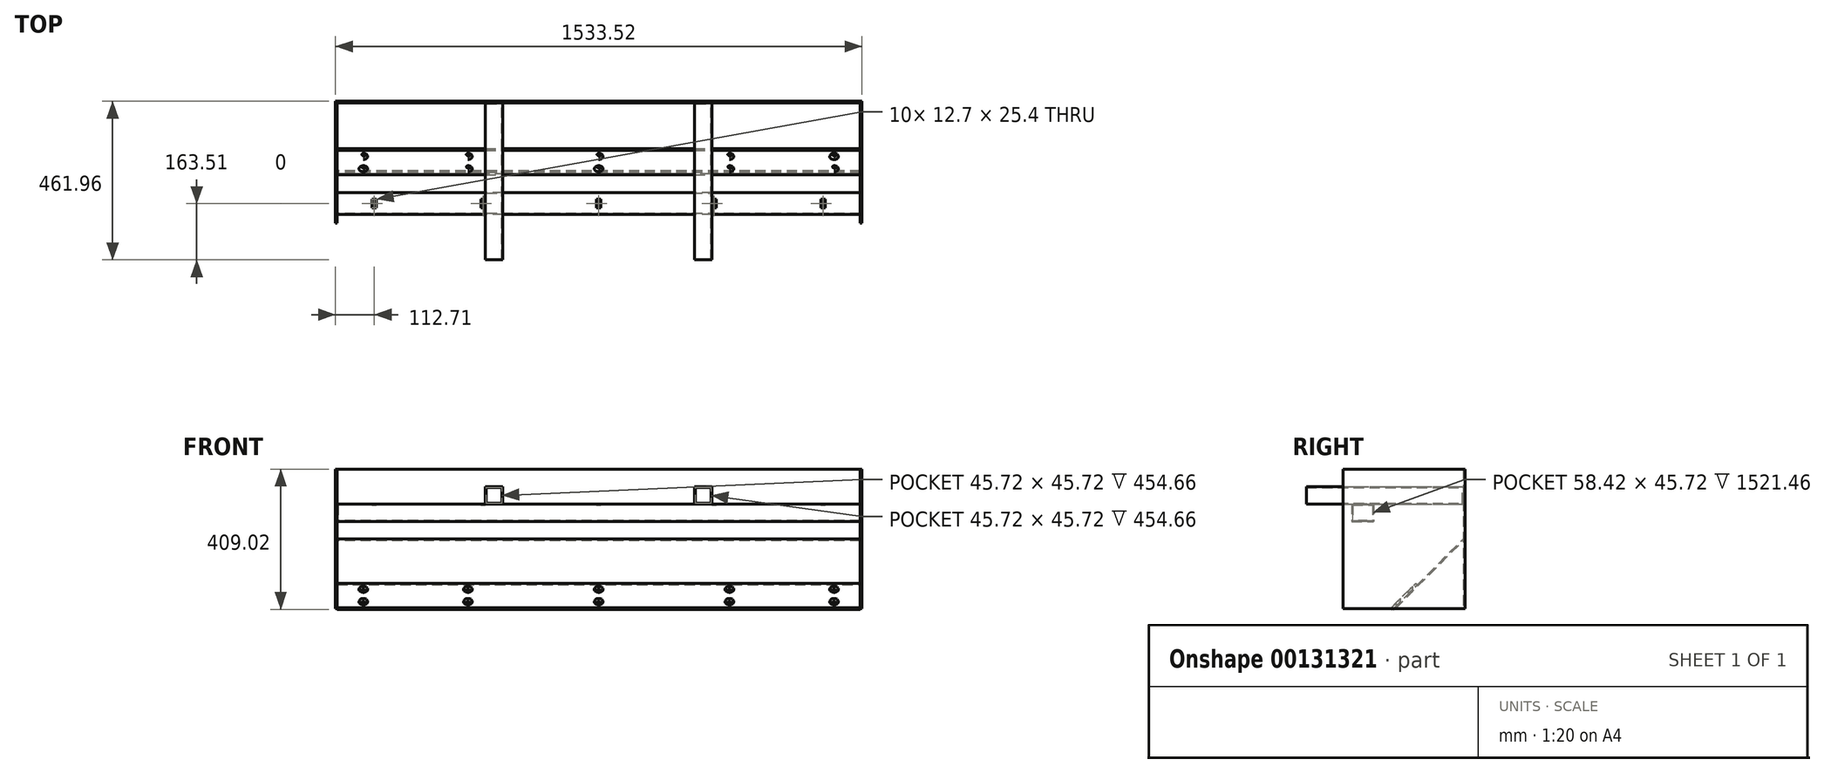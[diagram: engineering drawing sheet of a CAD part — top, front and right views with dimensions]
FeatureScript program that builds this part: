
annotation { "Feature Type Name" : "Feature", "Feature Type Description" : "" }
export const myFeature = defineFeature(function(context is Context, id is Id, definition is map)
    precondition{}
    {
        {
            var Q0;
            Q0=qCreatedBy(makeId("Front.planeOp"),FACE);
            var sketch = newSketch(context, id + "F0", { "sketchPlane" : qUnion([Q0])});
            skLineSegment(sketch, "E0.bottom", {"start": v(0, 406.4) * mm, "end": v(1524, 406.4) * mm});
            skLineSegment(sketch, "E0.top", {"start": v(0, 0) * mm, "end": v(1524, 0) * mm});
            skLineSegment(sketch, "E0.left", {"start": v(0, 406.4) * mm, "end": v(0, 0) * mm});
            skLineSegment(sketch, "E0.right", {"start": v(1524, 406.4) * mm, "end": v(1524, 0) * mm});
            skSolve(sketch);
        }
        {
            var Q0;
            Q0=makeQuery(id+"F0.imprint","IMPRINT",FACE,{"disambiguationData":[TD([[makeQuery(id+"F0.imprint","IMPRINT",EDGE,{"derivedFrom":sQuery(id+"F0.wireOp",EDGE,"E0.bottom")}),-1.0]])]});
            extrude(context, id + "F1", {"entities" : qUnion([Q0]), "depth" : 4.76 * mm});
        }
        {
            var Q0;
            Q0=makeQuery(id+"F1.opExtrude","SWEPT_FACE",FACE,{"disambiguationData":[OSD([sQuery(id+"F0.wireOp",EDGE,"E0.left")])]});
            var sketch = newSketch(context, id + "F2", { "sketchPlane" : qUnion([Q0])});
            skLineSegment(sketch, "E1.bottom", {"start": v(0, 0) * mm, "end": v(355.6, 0) * mm});
            skLineSegment(sketch, "E1.top", {"start": v(0, 406.4) * mm, "end": v(355.6, 406.4) * mm});
            skLineSegment(sketch, "E1.left", {"start": v(0, 0) * mm, "end": v(0, 406.4) * mm});
            skLineSegment(sketch, "E1.right", {"start": v(355.6, 0) * mm, "end": v(355.6, 406.4) * mm});
            skSolve(sketch);
        }
        {
            var Q0;
            {var subQ2=sQuery(id+"F2.wireOp",EDGE,"E1.right");Q0=makeQuery(id+"F2.imprint","IMPRINT",FACE,{"disambiguationData":[TD([[makeQuery(id+"F2.imprint","IMPRINT",EDGE,{"derivedFrom":subQ2}),1.0]])]});}
            var Q1;
            {var subQ0=sQuery(id+"F2.wireOp",EDGE,"E1.left");Q1=makeQuery(id+"F2.imprint","IMPRINT",FACE,{"disambiguationData":[TD([[makeQuery(id+"F2.imprint","IMPRINT",EDGE,{"derivedFrom":subQ0}),1.0]])]});}
            extrude(context, id + "F3", {"entities" : qUnion([Q0, Q1]), "operationType" : NewBodyOperationType.ADD, "depth" : 4.76 * mm});
        }
        {
            var Q0;
            Q0=makeQuery(id+"F1.opExtrude","SWEPT_FACE",FACE,{"disambiguationData":[OSD([sQuery(id+"F0.wireOp",EDGE,"E0.right")])]});
            var sketch = newSketch(context, id + "F4", { "sketchPlane" : qUnion([Q0])});
            skLineSegment(sketch, "E2.bottom", {"start": v(0, 0) * mm, "end": v(-355.6, 0) * mm});
            skLineSegment(sketch, "E2.top", {"start": v(0, 406.4) * mm, "end": v(-355.6, 406.4) * mm});
            skLineSegment(sketch, "E2.left", {"start": v(0, 0) * mm, "end": v(0, 406.4) * mm});
            skLineSegment(sketch, "E2.right", {"start": v(-355.6, 0) * mm, "end": v(-355.6, 406.4) * mm});
            skSolve(sketch);
        }
        {
            var Q0;
            {var subQ2=sQuery(id+"F4.wireOp",EDGE,"E2.right");Q0=makeQuery(id+"F4.imprint","IMPRINT",FACE,{"disambiguationData":[TD([[makeQuery(id+"F4.imprint","IMPRINT",EDGE,{"derivedFrom":subQ2}),-1.0]])]});}
            var Q1;
            {var subQ0=sQuery(id+"F4.wireOp",EDGE,"E2.left");Q1=makeQuery(id+"F4.imprint","IMPRINT",FACE,{"disambiguationData":[TD([[makeQuery(id+"F4.imprint","IMPRINT",EDGE,{"derivedFrom":subQ0}),-1.0]])]});}
            extrude(context, id + "F5", {"entities" : qUnion([Q0, Q1]), "operationType" : NewBodyOperationType.ADD, "depth" : 4.76 * mm});
        }
        {
            var Q0;
            Q0=makeQuery(id+"F3.opExtrude","CAP_FACE",FACE,{"disambiguationData":[OSD([sQuery(id+"F2.wireOp",EDGE,"E1.bottom"),sQuery(id+"F2.wireOp",EDGE,"E1.top"),sQuery(id+"F2.wireOp",EDGE,"E1.left"),sQuery(id+"F2.wireOp",EDGE,"E1.right")])],"isStart":true});
            var sketch = newSketch(context, id + "F6", { "sketchPlane" : qUnion([Q0])});
            skLineSegment(sketch, "E3", {"start": v(-202.64, 0) * mm, "end": v(-4.76, 197.88) * mm});
            skLineSegment(sketch, "E4", {"start": v(-207.4, 0) * mm, "end": v(-4.76, 202.64) * mm});
            skLineSegment(sketch, "E5", {"start": v(-4.76, 202.64) * mm, "end": v(-4.76, 197.88) * mm});
            skLineSegment(sketch, "E6", {"start": v(-207.4, 0) * mm, "end": v(-202.64, 0) * mm});
            skSolve(sketch);
        }
        {
            var Q0;
            {var subQ0=sQuery(id+"F6.wireOp",EDGE,"E6");Q0=makeQuery(id+"F6.imprint","IMPRINT",FACE,{"disambiguationData":[TD([[makeQuery(id+"F6.imprint","IMPRINT",EDGE,{"derivedFrom":subQ0}),-1.0]])]});}
            var Q1;
            {var subQ0=sQuery(id+"F6.wireOp",EDGE,"E5");Q1=makeQuery(id+"F6.imprint","IMPRINT",FACE,{"disambiguationData":[TD([[makeQuery(id+"F6.imprint","IMPRINT",EDGE,{"derivedFrom":subQ0}),-1.0]])]});}
            extrude(context, id + "F7", {"entities" : qUnion([Q0, Q1]), "depth" : 1524 * mm});
        }
        {
            var Q0;
            {var subQ2=sQuery(id+"F2.wireOp",EDGE,"E1.right");Q0=makeQuery(id+"F2.imprint","IMPRINT",FACE,{"disambiguationData":[TD([[makeQuery(id+"F2.imprint","IMPRINT",EDGE,{"derivedFrom":subQ2}),1.0]])]});}
            var sketch = newSketch(context, id + "F8", { "sketchPlane" : qUnion([Q0])});
            skLineSegment(sketch, "E7.bottom", {"start": v(330.2, 304.8) * mm, "end": v(266.7, 304.8) * mm});
            skLineSegment(sketch, "E7.top", {"start": v(330.2, 254) * mm, "end": v(266.7, 254) * mm});
            skLineSegment(sketch, "E7.left", {"start": v(330.2, 304.8) * mm, "end": v(330.2, 254) * mm});
            skLineSegment(sketch, "E7.right", {"start": v(266.7, 304.8) * mm, "end": v(266.7, 254) * mm});
            skSolve(sketch);
        }
        {
            var Q0;
            Q0=makeQuery(id+"F8.imprint","IMPRINT",FACE,{"disambiguationData":[TD([[makeQuery(id+"F8.imprint","IMPRINT",EDGE,{"derivedFrom":sQuery(id+"F8.wireOp",EDGE,"E7.bottom")}),1.0]])]});
            extrude(context, id + "F9", {"entities" : qUnion([Q0]), "oppositeDirection" : true, "depth" : 1524 * mm});
        }
        {
            var Q0;
            Q0=makeQuery(id+"F7.opExtrude","SWEPT_FACE",FACE,{"disambiguationData":[OSD([sQuery(id+"F6.wireOp",EDGE,"E4")])]});
            var sketch = newSketch(context, id + "F10", { "sketchPlane" : qUnion([Q0])});
            skLineSegment(sketch, "E8.bottom", {"start": v(0, -48.76) * mm, "end": v(1524, -48.76) * mm});
            skLineSegment(sketch, "E8.top", {"start": v(0, -150.36) * mm, "end": v(1524, -150.36) * mm});
            skLineSegment(sketch, "E8.left", {"start": v(0, -48.76) * mm, "end": v(0, -150.36) * mm});
            skLineSegment(sketch, "E8.right", {"start": v(1524, -48.76) * mm, "end": v(1524, -150.36) * mm});
            skSolve(sketch);
        }
        {
            var Q0;
            {var subQ0=sQuery(id+"F10.wireOp",EDGE,"E8.bottom");Q0=makeQuery(id+"F10.imprint","IMPRINT",FACE,{"disambiguationData":[TD([[makeQuery(id+"F10.imprint","IMPRINT",EDGE,{"derivedFrom":subQ0}),-1.0]])]});}
            var Q1;
            {var subQ0=sQuery(id+"F10.wireOp",EDGE,"E8.top");Q1=makeQuery(id+"F10.imprint","IMPRINT",FACE,{"disambiguationData":[TD([[makeQuery(id+"F10.imprint","IMPRINT",EDGE,{"derivedFrom":subQ0}),1.0]])]});}
            extrude(context, id + "F11", {"entities" : qUnion([Q0, Q1]), "depth" : 6.35 * mm});
        }
        {
            var Q0;
            Q0=makeQuery(id+"F11.opExtrude","CAP_FACE",FACE,{"disambiguationData":[OSD([sQuery(id+"F10.wireOp",EDGE,"E8.bottom"),sQuery(id+"F10.wireOp",EDGE,"E8.top"),sQuery(id+"F10.wireOp",EDGE,"E8.left"),sQuery(id+"F10.wireOp",EDGE,"E8.right")])],"isStart":false});
            var sketch = newSketch(context, id + "F12", { "sketchPlane" : qUnion([Q0])});
            skLineSegment(sketch, "E9", {"start": v(0, -74.16) * mm, "end": v(1524, -74.16) * mm, "construction": true});
            skLineSegment(sketch, "E10", {"start": v(0, -124.96) * mm, "end": v(1524, -124.96) * mm, "construction": true});
            skPoint(sketch, "E11", {"position": v(76.2, -74.16) * mm});
            skPoint(sketch, "E12", {"position": v(381, -74.16) * mm});
            skPoint(sketch, "E13", {"position": v(762, -74.16) * mm});
            skPoint(sketch, "E14", {"position": v(1143, -74.16) * mm});
            skPoint(sketch, "E15", {"position": v(1447.8, -74.16) * mm});
            skPoint(sketch, "E16", {"position": v(76.2, -124.96) * mm});
            skPoint(sketch, "E17", {"position": v(381, -124.96) * mm});
            skPoint(sketch, "E18", {"position": v(762, -124.96) * mm});
            skPoint(sketch, "E19", {"position": v(1143, -124.96) * mm});
            skPoint(sketch, "E20", {"position": v(1447.8, -124.96) * mm});
            skSolve(sketch);
        }
        {
            var Q0;
            Q0=sQuery(id+"F12.wireOp",VERTEX,"E11");
            var Q1;
            Q1=sQuery(id+"F12.wireOp",VERTEX,"E16");
            var Q2;
            Q2=sQuery(id+"F12.wireOp",VERTEX,"E12");
            var Q3;
            Q3=sQuery(id+"F12.wireOp",VERTEX,"E17");
            var Q4;
            Q4=sQuery(id+"F12.wireOp",VERTEX,"E13");
            var Q5;
            Q5=sQuery(id+"F12.wireOp",VERTEX,"E18");
            var Q6;
            Q6=sQuery(id+"F12.wireOp",VERTEX,"E14");
            var Q7;
            Q7=sQuery(id+"F12.wireOp",VERTEX,"E19");
            var Q8;
            Q8=sQuery(id+"F12.wireOp",VERTEX,"E15");
            var Q9;
            Q9=sQuery(id+"F12.wireOp",VERTEX,"E20");
            var Q10;
            Q10=makeQuery(id+"F11.opExtrude","SWEPT_BODY",BODY,{"disambiguationData":[OSD([sQuery(id+"F10.wireOp",EDGE,"E8.bottom"),sQuery(id+"F10.wireOp",EDGE,"E8.top"),sQuery(id+"F10.wireOp",EDGE,"E8.left"),sQuery(id+"F10.wireOp",EDGE,"E8.right")])]});
            var Q11;
            Q11=makeQuery(id+"F7.opExtrude","SWEPT_BODY",BODY,{"disambiguationData":[OSD([sQuery(id+"F6.wireOp",EDGE,"E3"),sQuery(id+"F6.wireOp",EDGE,"E4"),sQuery(id+"F6.wireOp",EDGE,"E5"),sQuery(id+"F6.wireOp",EDGE,"E6")])]});
            hole(context, id + "F13", {"style" : HoleStyle.C_SINK, "endStyle" : HoleEndStyle.THROUGH, "holeDiameter" : 9.52 * mm, "cSinkDiameter" : 25.4 * mm, "cSinkAngle" : 90 * degree, "locations" : qUnion([Q0, Q1, Q2, Q3, Q4, Q5, Q6, Q7, Q8, Q9]), "scope" : qUnion([Q10, Q11]), "isTappedThrough" : true});
        }
        {
            var Q0;
            Q0=makeQuery(id+"F9.opExtrude","CAP_FACE",FACE,{"disambiguationData":[OSD([sQuery(id+"F8.wireOp",EDGE,"E7.bottom"),sQuery(id+"F8.wireOp",EDGE,"E7.top"),sQuery(id+"F8.wireOp",EDGE,"E7.left"),sQuery(id+"F8.wireOp",EDGE,"E7.right")])],"isStart":false});
            shell(context, id + "F14", {"entities" : qUnion([Q0]), "thickness" : 2.54 * mm});
        }
        {
            var Q0;
            Q0=makeQuery(id+"F9.opExtrude","SWEPT_FACE",FACE,{"disambiguationData":[OSD([sQuery(id+"F8.wireOp",EDGE,"E7.bottom")])]});
            var sketch = newSketch(context, id + "F15", { "sketchPlane" : qUnion([Q0])});
            skLineSegment(sketch, "E21.bottom", {"start": v(101.6, -285.75) * mm, "end": v(114.3, -285.75) * mm});
            skLineSegment(sketch, "E21.top", {"start": v(101.6, -311.15) * mm, "end": v(114.3, -311.15) * mm});
            skLineSegment(sketch, "E21.left", {"start": v(101.6, -285.75) * mm, "end": v(101.6, -311.15) * mm});
            skLineSegment(sketch, "E21.right", {"start": v(114.3, -285.75) * mm, "end": v(114.3, -311.15) * mm});
            skLineSegment(sketch, "E22.bottom", {"start": v(419.1, -285.75) * mm, "end": v(431.8, -285.75) * mm});
            skLineSegment(sketch, "E22.top", {"start": v(419.1, -311.15) * mm, "end": v(431.8, -311.15) * mm});
            skLineSegment(sketch, "E22.left", {"start": v(431.8, -285.75) * mm, "end": v(431.8, -311.15) * mm});
            skLineSegment(sketch, "E22.right", {"start": v(419.1, -285.75) * mm, "end": v(419.1, -311.15) * mm});
            skLineSegment(sketch, "E23.bottom", {"start": v(1409.7, -285.75) * mm, "end": v(1422.4, -285.75) * mm});
            skLineSegment(sketch, "E23.top", {"start": v(1409.7, -311.15) * mm, "end": v(1422.4, -311.15) * mm});
            skLineSegment(sketch, "E23.left", {"start": v(1422.4, -285.75) * mm, "end": v(1422.4, -311.15) * mm});
            skLineSegment(sketch, "E23.right", {"start": v(1409.7, -285.75) * mm, "end": v(1409.7, -311.15) * mm});
            skLineSegment(sketch, "E24.bottom", {"start": v(1092.2, -285.75) * mm, "end": v(1104.9, -285.75) * mm});
            skLineSegment(sketch, "E24.top", {"start": v(1092.2, -311.15) * mm, "end": v(1104.9, -311.15) * mm});
            skLineSegment(sketch, "E24.left", {"start": v(1092.2, -285.75) * mm, "end": v(1092.2, -311.15) * mm});
            skLineSegment(sketch, "E24.right", {"start": v(1104.9, -285.75) * mm, "end": v(1104.9, -311.15) * mm});
            skLineSegment(sketch, "E25", {"start": v(1016, -330.2) * mm, "end": v(1016.42, -329.56) * mm});
            skLineSegment(sketch, "E26.bottom", {"start": v(755.65, -285.16) * mm, "end": v(768.35, -285.16) * mm});
            skLineSegment(sketch, "E26.top", {"start": v(755.65, -310.56) * mm, "end": v(768.35, -310.56) * mm});
            skLineSegment(sketch, "E26.left", {"start": v(755.65, -285.16) * mm, "end": v(755.65, -310.56) * mm});
            skLineSegment(sketch, "E26.right", {"start": v(768.35, -285.16) * mm, "end": v(768.35, -310.56) * mm});
            skLineSegment(sketch, "E27", {"start": v(762, -285.16) * mm, "end": v(762, -266.7) * mm});
            skSolve(sketch);
        }
        {
            var Q0;
            {var subQ3=sQuery(id+"F15.wireOp",EDGE,"E21.left");Q0=makeQuery(id+"F15.imprint","IMPRINT",FACE,{"disambiguationData":[TD([[makeQuery(id+"F15.imprint","IMPRINT",EDGE,{"derivedFrom":subQ3}),1.0]])]});}
            var Q1;
            {var subQ0=sQuery(id+"F15.wireOp",EDGE,"E22.left");Q1=makeQuery(id+"F15.imprint","IMPRINT",FACE,{"disambiguationData":[TD([[makeQuery(id+"F15.imprint","IMPRINT",EDGE,{"derivedFrom":subQ0}),-1.0]])]});}
            var Q2;
            {var subQ3=sQuery(id+"F15.wireOp",EDGE,"E24.left");Q2=makeQuery(id+"F15.imprint","IMPRINT",FACE,{"disambiguationData":[TD([[makeQuery(id+"F15.imprint","IMPRINT",EDGE,{"derivedFrom":subQ3}),1.0]])]});}
            var Q3;
            {var subQ0=sQuery(id+"F15.wireOp",EDGE,"E23.left");Q3=makeQuery(id+"F15.imprint","IMPRINT",FACE,{"disambiguationData":[TD([[makeQuery(id+"F15.imprint","IMPRINT",EDGE,{"derivedFrom":subQ0}),-1.0]])]});}
            var Q4;
            Q4=makeQuery(id+"F15.imprint","IMPRINT",FACE,{"disambiguationData":[TD([[makeQuery(id+"F15.imprint","IMPRINT",EDGE,{"derivedFrom":sQuery(id+"F15.wireOp",EDGE,"E26.bottom")}),-1.0]])]});
            extrude(context, id + "F16", {"entities" : qUnion([Q0, Q1, Q2, Q3, Q4]), "operationType" : NewBodyOperationType.REMOVE, "endBound" : BoundingType.THROUGH_ALL, "oppositeDirection" : true, "depth" : 25.4 * mm});
        }
        {
            var Q0;
            Q0=makeQuery(id+"F1.opExtrude","CAP_FACE",FACE,{"disambiguationData":[OSD([sQuery(id+"F0.wireOp",EDGE,"E0.bottom"),sQuery(id+"F0.wireOp",EDGE,"E0.top"),sQuery(id+"F0.wireOp",EDGE,"E0.left"),sQuery(id+"F0.wireOp",EDGE,"E0.right")])],"isStart":false});
            var sketch = newSketch(context, id + "F17", { "sketchPlane" : qUnion([Q0])});
            skLineSegment(sketch, "E28.bottom", {"start": v(431.8, 304.8) * mm, "end": v(482.6, 304.8) * mm});
            skLineSegment(sketch, "E28.top", {"start": v(431.8, 355.6) * mm, "end": v(482.6, 355.6) * mm});
            skLineSegment(sketch, "E28.left", {"start": v(431.8, 304.8) * mm, "end": v(431.8, 355.6) * mm});
            skLineSegment(sketch, "E28.right", {"start": v(482.6, 304.8) * mm, "end": v(482.6, 355.6) * mm});
            skLineSegment(sketch, "E29.bottom", {"start": v(1041.4, 304.8) * mm, "end": v(1092.2, 304.8) * mm});
            skLineSegment(sketch, "E29.top", {"start": v(1041.4, 355.6) * mm, "end": v(1092.2, 355.6) * mm});
            skLineSegment(sketch, "E29.left", {"start": v(1041.4, 304.8) * mm, "end": v(1041.4, 355.6) * mm});
            skLineSegment(sketch, "E29.right", {"start": v(1092.2, 304.8) * mm, "end": v(1092.2, 355.6) * mm});
            skLineSegment(sketch, "E30", {"start": v(431.8, 330.2) * mm, "end": v(0, 330.2) * mm});
            skLineSegment(sketch, "E31", {"start": v(1092.2, 330.2) * mm, "end": v(1524, 330.2) * mm});
            skSolve(sketch);
        }
        {
            var Q0;
            {var subQ3=sQuery(id+"F17.wireOp",EDGE,"E28.bottom");Q0=makeQuery(id+"F17.imprint","IMPRINT",FACE,{"disambiguationData":[TD([[makeQuery(id+"F17.imprint","IMPRINT",EDGE,{"derivedFrom":subQ3}),1.0]])]});}
            var Q1;
            {var subQ1=sQuery(id+"F17.wireOp",EDGE,"E29.bottom");Q1=makeQuery(id+"F17.imprint","IMPRINT",FACE,{"disambiguationData":[TD([[makeQuery(id+"F17.imprint","IMPRINT",EDGE,{"derivedFrom":subQ1}),1.0]])]});}
            extrude(context, id + "F18", {"entities" : qUnion([Q0, Q1]), "depth" : 457.2 * mm});
        }
        {
            var Q0;
            Q0=makeQuery(id+"F18.opExtrude","CAP_FACE",FACE,{"disambiguationData":[OSD([sQuery(id+"F17.wireOp",EDGE,"E28.bottom"),sQuery(id+"F17.wireOp",EDGE,"E28.top"),sQuery(id+"F17.wireOp",EDGE,"E28.left"),sQuery(id+"F17.wireOp",EDGE,"E28.right")])],"isStart":false});
            var Q1;
            Q1=makeQuery(id+"F18.opExtrude","CAP_FACE",FACE,{"disambiguationData":[OSD([sQuery(id+"F17.wireOp",EDGE,"E29.bottom"),sQuery(id+"F17.wireOp",EDGE,"E29.top"),sQuery(id+"F17.wireOp",EDGE,"E29.left"),sQuery(id+"F17.wireOp",EDGE,"E29.right")])],"isStart":false});
            shell(context, id + "F19", {"entities" : qUnion([Q0, Q1]), "thickness" : 2.54 * mm});
        }
    });
